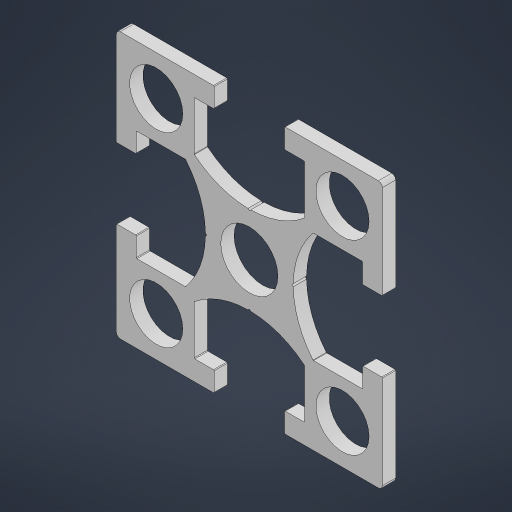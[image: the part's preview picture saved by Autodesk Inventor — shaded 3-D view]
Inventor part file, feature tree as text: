
AUTODESK INVENTOR PART (.ipt)
format: ipt  version: 2024 (Build 280153000, 153)  size: 324,608 bytes
history: native  units: mm
features: other x1, extrude x1, fillet x1, sketch x1
ambient origin geometry x8: Origin, YZ Plane, XZ Plane, XY Plane, X Axis, Y Axis, Z Axis, Center Point
bodies: Body1 (feature_tree)
feature tree (4):
  other  "솔리드1"
  extrude  "프로파일 길이 설정"  Depth=20.0mm
  fillet  "모서리"  Radius=20.0mm
  sketch  "스케치1"
